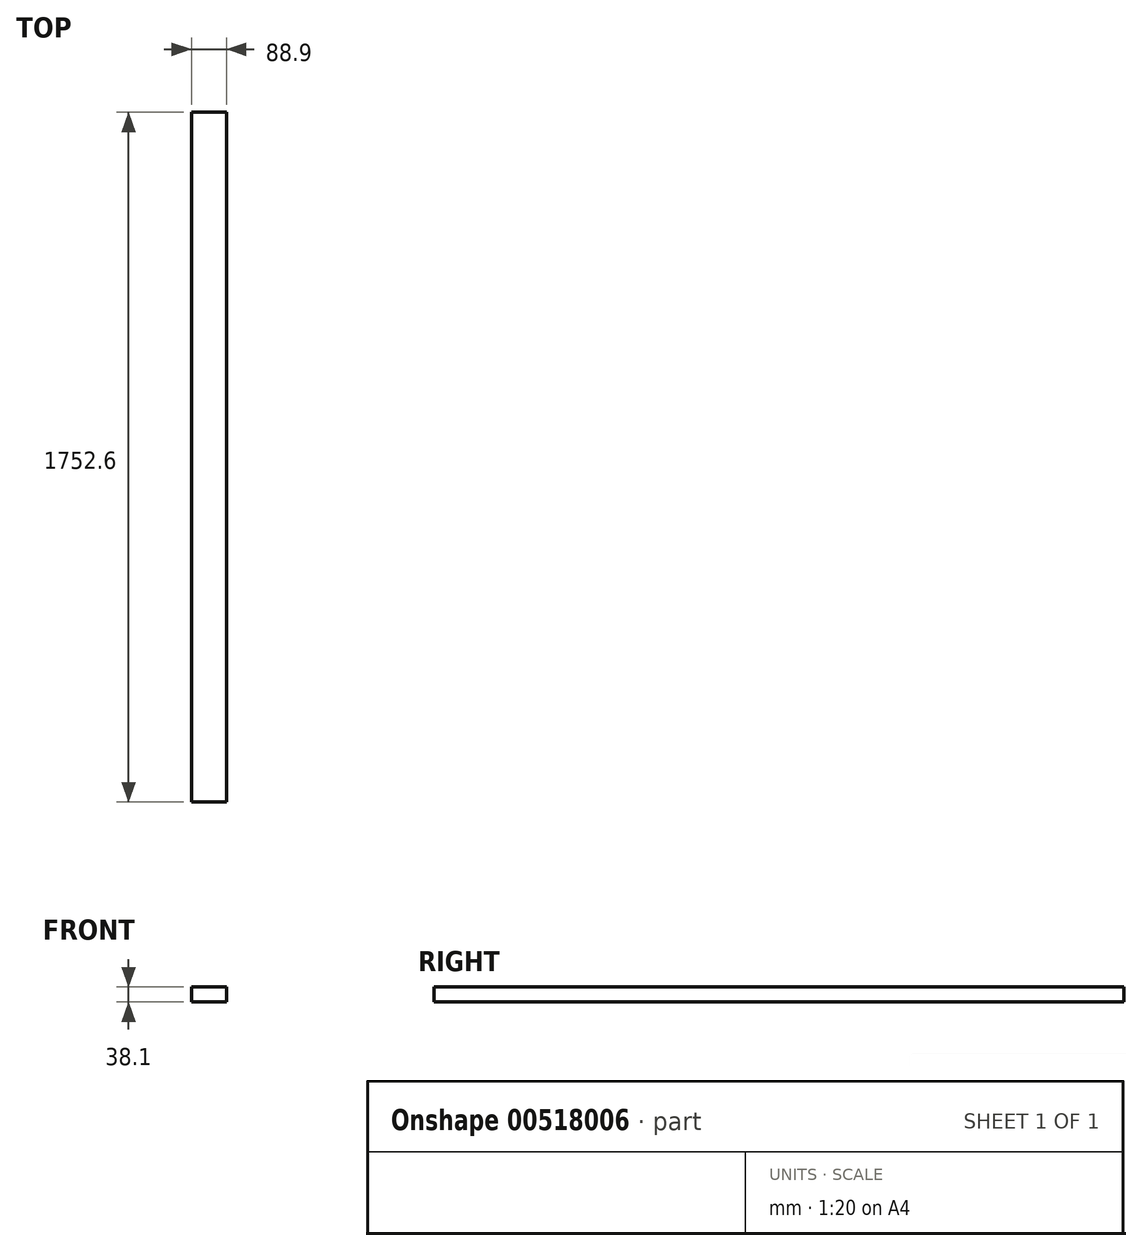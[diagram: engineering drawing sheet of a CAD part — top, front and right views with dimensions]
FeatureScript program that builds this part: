
annotation { "Feature Type Name" : "Feature", "Feature Type Description" : "" }
export const myFeature = defineFeature(function(context is Context, id is Id, definition is map)
    precondition{}
    {
        {
            var Q0;
            Q0=qCreatedBy(makeId("Front.planeOp"),FACE);
            var sketch = newSketch(context, id + "F0", { "sketchPlane" : qUnion([Q0])});
            skLineSegment(sketch, "E0.bottom", {"start": v(0, 0) * mm, "end": v(88.9, 0) * mm});
            skLineSegment(sketch, "E0.top", {"start": v(0, 38.1) * mm, "end": v(88.9, 38.1) * mm});
            skLineSegment(sketch, "E0.left", {"start": v(0, 0) * mm, "end": v(0, 38.1) * mm});
            skLineSegment(sketch, "E0.right", {"start": v(88.9, 0) * mm, "end": v(88.9, 38.1) * mm});
            skSolve(sketch);
        }
        {
            var Q0;
            Q0=qSketchRegion(id+"F0",true);
            extrude(context, id + "F1", {"entities" : qUnion([Q0]), "depth" : 1752.6 * mm, "offsetDistance" : 25 * mm});
        }
    });
